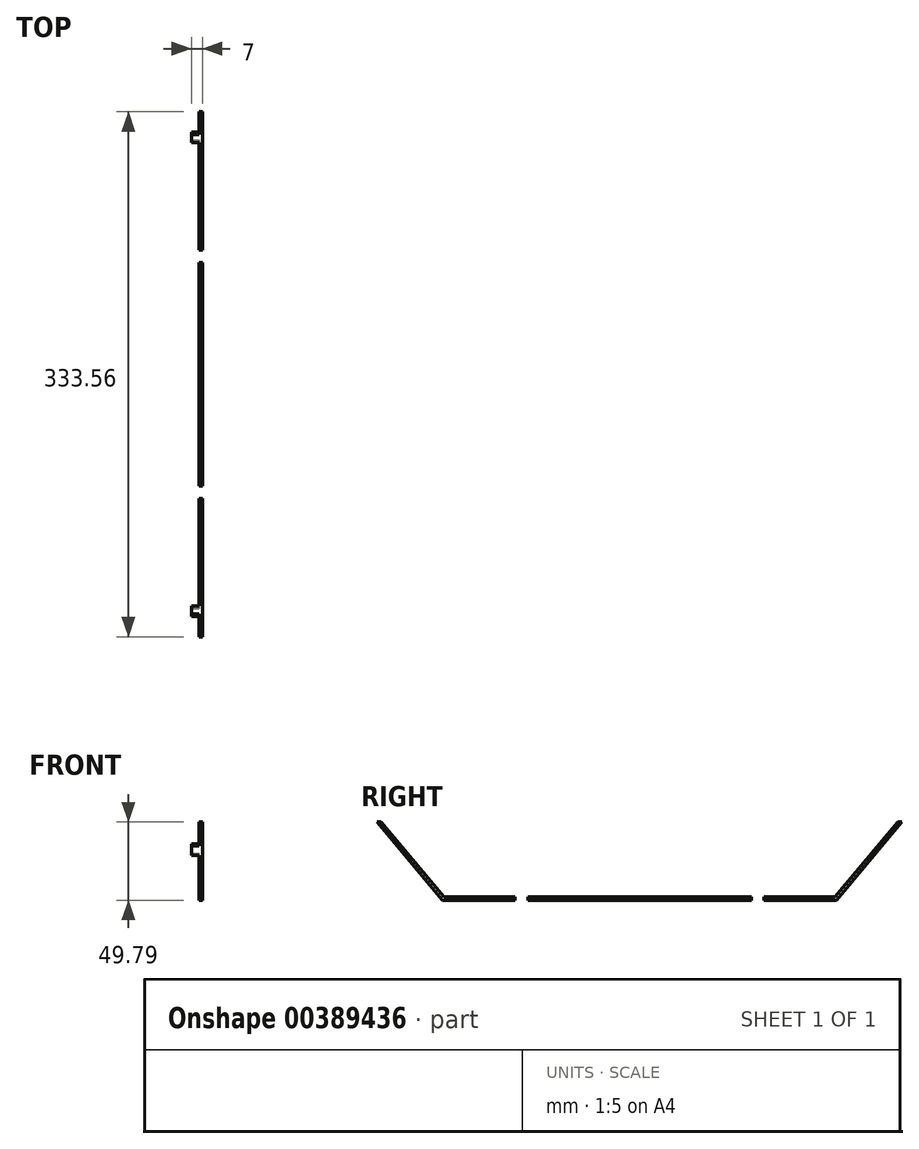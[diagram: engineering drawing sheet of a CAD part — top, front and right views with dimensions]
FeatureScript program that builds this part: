
annotation { "Feature Type Name" : "Feature", "Feature Type Description" : "" }
export const myFeature = defineFeature(function(context is Context, id is Id, definition is map)
    precondition{}
    {
        {
            var Q0;
            Q0=qCreatedBy(makeId("Right.planeOp"),FACE);
            var sketch = newSketch(context, id + "F0", { "sketchPlane" : qUnion([Q0])});
            skLineSegment(sketch, "E0", {"start": v(0, 0) * mm, "end": v(-248.13, 0) * mm});
            skLineSegment(sketch, "E1", {"start": v(-248.13, 0) * mm, "end": v(-288.24, 47.8) * mm});
            skLineSegment(sketch, "E2", {"start": v(0, 0) * mm, "end": v(40.1, 47.8) * mm});
            skLineSegment(sketch, "E3.0", {"start": v(0.93, -2) * mm, "end": v(42.71, 47.8) * mm});
            skLineSegment(sketch, "E3.1", {"start": v(0.93, -2) * mm, "end": v(-249.07, -2) * mm});
            skLineSegment(sketch, "E3.2", {"start": v(-249.07, -2) * mm, "end": v(-290.85, 47.8) * mm});
            skLineSegment(sketch, "E4", {"start": v(-290.85, 47.8) * mm, "end": v(-288.24, 47.8) * mm});
            skLineSegment(sketch, "E5", {"start": v(42.71, 47.8) * mm, "end": v(40.1, 47.8) * mm});
            skLineSegment(sketch, "E6.bottom", {"start": v(-45.07, 0) * mm, "end": v(-53.07, 0) * mm});
            skLineSegment(sketch, "E6.top", {"start": v(-45.07, -2) * mm, "end": v(-53.07, -2) * mm});
            skLineSegment(sketch, "E6.left", {"start": v(-45.07, 0) * mm, "end": v(-45.07, -2) * mm});
            skLineSegment(sketch, "E6.right", {"start": v(-53.07, 0) * mm, "end": v(-53.07, -2) * mm});
            skLineSegment(sketch, "E7.bottom", {"start": v(-195.07, 0) * mm, "end": v(-203.07, 0) * mm});
            skLineSegment(sketch, "E7.top", {"start": v(-195.07, -2) * mm, "end": v(-203.07, -2) * mm});
            skLineSegment(sketch, "E7.left", {"start": v(-195.07, 0) * mm, "end": v(-195.07, -2) * mm});
            skLineSegment(sketch, "E7.right", {"start": v(-203.07, 0) * mm, "end": v(-203.07, -2) * mm});
            skLineSegment(sketch, "E8", {"start": v(-278, 32.47) * mm, "end": v(-276.46, 33.76) * mm});
            skLineSegment(sketch, "E9", {"start": v(-272.85, 26.34) * mm, "end": v(-271.32, 27.63) * mm});
            skLineSegment(sketch, "E10", {"start": v(24.72, 26.34) * mm, "end": v(23.18, 27.63) * mm});
            skLineSegment(sketch, "E11", {"start": v(28.33, 33.76) * mm, "end": v(29.86, 32.47) * mm});
            skLineSegment(sketch, "E12", {"start": v(-288.24, 47.8) * mm, "end": v(40.1, 47.8) * mm});
            skSolve(sketch);
        }
        {
            var Q0;
            {var subQ0=sQuery(id+"F0.wireOp",EDGE,"E6.right");Q0=makeQuery(id+"F0.imprint","IMPRINT",FACE,{"disambiguationData":[TD([[makeQuery(id+"F0.imprint","IMPRINT",EDGE,{"derivedFrom":subQ0}),-1.0]])]});}
            var Q1;
            Q1=makeQuery(id+"F0.imprint","IMPRINT",FACE,{"disambiguationData":[TD([[makeQuery(id+"F0.imprint","IMPRINT",EDGE,{"derivedFrom":sQuery(id+"F0.wireOp",EDGE,"E6.bottom")}),1.0]])]});
            var Q2;
            {var subQ4=sQuery(id+"F0.wireOp",EDGE,"E7.right");Q2=makeQuery(id+"F0.imprint","IMPRINT",FACE,{"disambiguationData":[TD([[makeQuery(id+"F0.imprint","IMPRINT",EDGE,{"derivedFrom":subQ4}),-1.0]])]});}
            var Q3;
            Q3=makeQuery(id+"F0.imprint","IMPRINT",FACE,{"disambiguationData":[TD([[makeQuery(id+"F0.imprint","IMPRINT",EDGE,{"derivedFrom":sQuery(id+"F0.wireOp",EDGE,"E7.bottom")}),1.0]])]});
            var Q4;
            {var subQ0=sQuery(id+"F0.wireOp",EDGE,"E4");Q4=makeQuery(id+"F0.imprint","IMPRINT",FACE,{"disambiguationData":[TD([[makeQuery(id+"F0.imprint","IMPRINT",EDGE,{"derivedFrom":subQ0}),-1.0]])]});}
            var Q5;
            {var subQ0=sQuery(id+"F0.wireOp",EDGE,"E8");Q5=makeQuery(id+"F0.imprint","IMPRINT",FACE,{"disambiguationData":[TD([[makeQuery(id+"F0.imprint","IMPRINT",EDGE,{"derivedFrom":subQ0}),-1.0]])]});}
            var Q6;
            {var subQ3=sQuery(id+"F0.wireOp",EDGE,"E6.left");Q6=makeQuery(id+"F0.imprint","IMPRINT",FACE,{"disambiguationData":[TD([[makeQuery(id+"F0.imprint","IMPRINT",EDGE,{"derivedFrom":subQ3}),1.0]])]});}
            var Q7;
            {var subQ0=sQuery(id+"F0.wireOp",EDGE,"E6.bottom");Q7=makeQuery(id+"F0.imprint","IMPRINT",FACE,{"disambiguationData":[TD([[makeQuery(id+"F0.imprint","IMPRINT",EDGE,{"derivedFrom":subQ0}),-1.0]])]});}
            var Q8;
            {var subQ0=sQuery(id+"F0.wireOp",EDGE,"E10");Q8=makeQuery(id+"F0.imprint","IMPRINT",FACE,{"disambiguationData":[TD([[makeQuery(id+"F0.imprint","IMPRINT",EDGE,{"derivedFrom":subQ0}),-1.0]])]});}
            var Q9;
            {var subQ0=sQuery(id+"F0.wireOp",EDGE,"E5");Q9=makeQuery(id+"F0.imprint","IMPRINT",FACE,{"disambiguationData":[TD([[makeQuery(id+"F0.imprint","IMPRINT",EDGE,{"derivedFrom":subQ0}),1.0]])]});}
            extrude(context, id + "F1", {"entities" : qUnion([Q0, Q1, Q2, Q3, Q4, Q5, Q6, Q7, Q8, Q9]), "depth" : 2 * mm});
        }
        {
            var Q0;
            Q0=makeQuery(id+"F0.imprint","IMPRINT",FACE,{"disambiguationData":[TD([[makeQuery(id+"F0.imprint","IMPRINT",EDGE,{"derivedFrom":sQuery(id+"F0.wireOp",EDGE,"E6.bottom")}),1.0]])]});
            var Q1;
            Q1=makeQuery(id+"F0.imprint","IMPRINT",FACE,{"disambiguationData":[TD([[makeQuery(id+"F0.imprint","IMPRINT",EDGE,{"derivedFrom":sQuery(id+"F0.wireOp",EDGE,"E7.bottom")}),1.0]])]});
            var Q2;
            {var subQ0=sQuery(id+"F0.wireOp",EDGE,"E8");Q2=makeQuery(id+"F0.imprint","IMPRINT",FACE,{"disambiguationData":[TD([[makeQuery(id+"F0.imprint","IMPRINT",EDGE,{"derivedFrom":subQ0}),-1.0]])]});}
            var Q3;
            {var subQ0=sQuery(id+"F0.wireOp",EDGE,"E10");Q3=makeQuery(id+"F0.imprint","IMPRINT",FACE,{"disambiguationData":[TD([[makeQuery(id+"F0.imprint","IMPRINT",EDGE,{"derivedFrom":subQ0}),-1.0]])]});}
            extrude(context, id + "F2", {"entities" : qUnion([Q0, Q1, Q2, Q3]), "operationType" : NewBodyOperationType.ADD, "oppositeDirection" : true, "depth" : 5 * mm});
        }
    });
